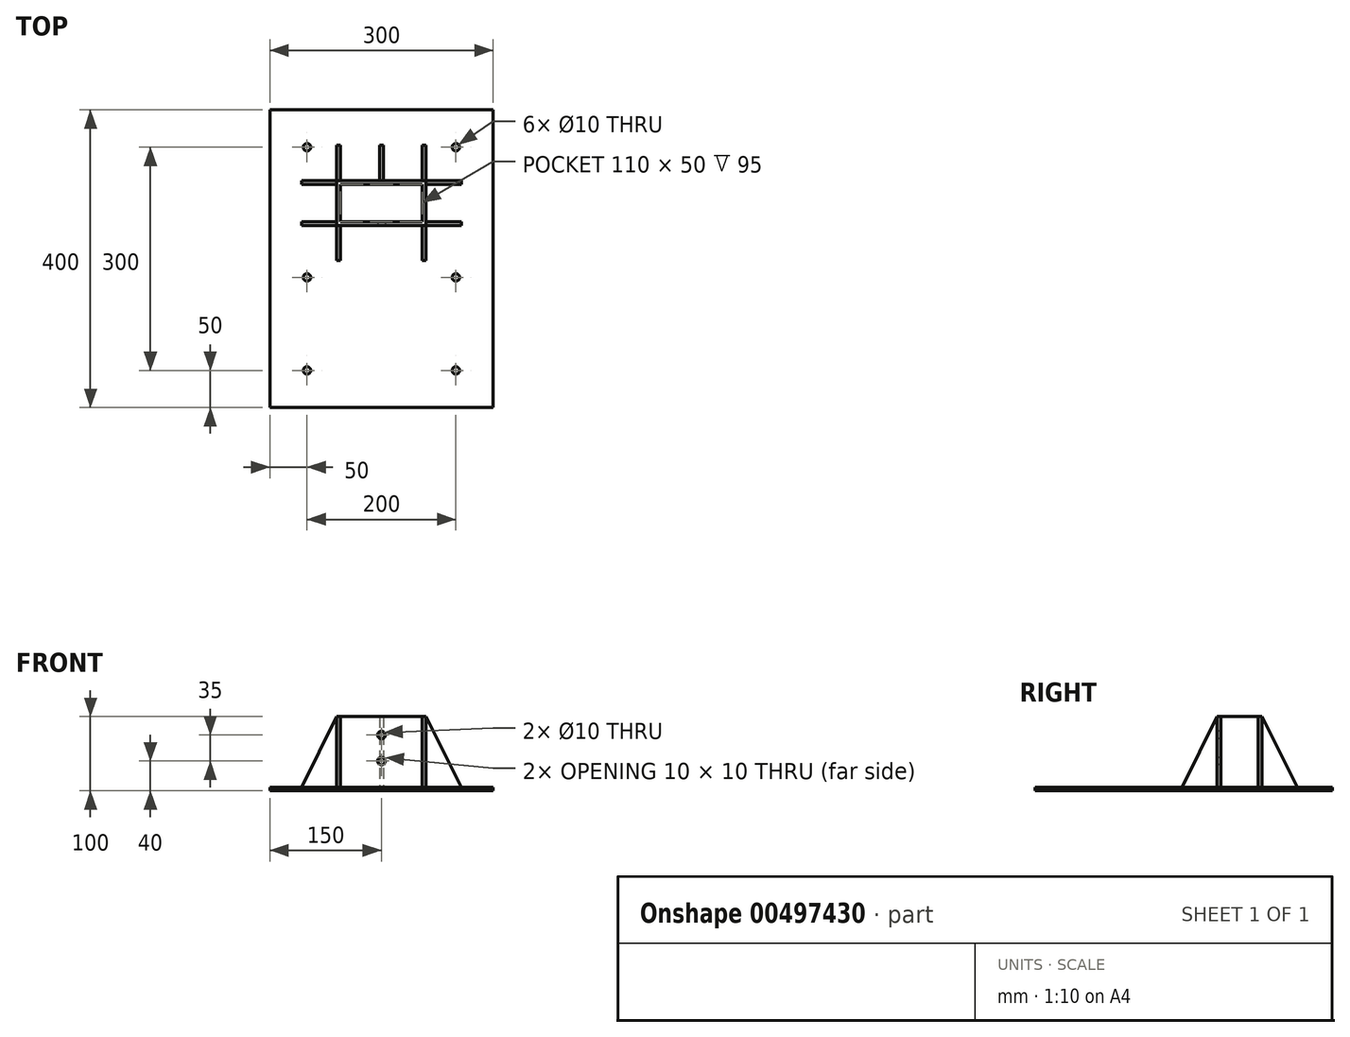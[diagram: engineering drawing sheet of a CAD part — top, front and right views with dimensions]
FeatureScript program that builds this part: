
annotation { "Feature Type Name" : "Feature", "Feature Type Description" : "" }
export const myFeature = defineFeature(function(context is Context, id is Id, definition is map)
    precondition{}
    {
        {
            var Q0;
            Q0=qCreatedBy(makeId("Top.planeOp"),FACE);
            var sketch = newSketch(context, id + "F0", { "sketchPlane" : qUnion([Q0])});
            skLineSegment(sketch, "E0.bottom", {"start": v(-150, -200) * mm, "end": v(150, -200) * mm});
            skLineSegment(sketch, "E0.top", {"start": v(-150, 200) * mm, "end": v(150, 200) * mm});
            skLineSegment(sketch, "E0.left", {"start": v(-150, -200) * mm, "end": v(-150, 200) * mm});
            skLineSegment(sketch, "E0.right", {"start": v(150, -200) * mm, "end": v(150, 200) * mm});
            skPoint(sketch, "E0.middle", {"position": v(0, 0) * mm});
            skLineSegment(sketch, "E1.bottom", {"start": v(-55, 50) * mm, "end": v(55, 50) * mm});
            skLineSegment(sketch, "E1.top", {"start": v(-55, 100) * mm, "end": v(55, 100) * mm});
            skLineSegment(sketch, "E1.left", {"start": v(-55, 50) * mm, "end": v(-55, 100) * mm});
            skLineSegment(sketch, "E1.right", {"start": v(55, 50) * mm, "end": v(55, 100) * mm});
            skPoint(sketch, "E1.middle", {"position": v(0, 75) * mm});
            skLineSegment(sketch, "E2.bottom", {"start": v(60, 45) * mm, "end": v(-60, 45) * mm});
            skLineSegment(sketch, "E2.top", {"start": v(60, 105) * mm, "end": v(-60, 105) * mm});
            skLineSegment(sketch, "E2.left", {"start": v(60, 45) * mm, "end": v(60, 105) * mm});
            skLineSegment(sketch, "E2.right", {"start": v(-60, 45) * mm, "end": v(-60, 105) * mm});
            skLineSegment(sketch, "E3", {"start": v(60, 105) * mm, "end": v(60, 155) * mm});
            skLineSegment(sketch, "E4", {"start": v(60, 155) * mm, "end": v(55, 155) * mm});
            skLineSegment(sketch, "E5", {"start": v(55, 155) * mm, "end": v(55, 100) * mm});
            skLineSegment(sketch, "E6", {"start": v(-60, 105) * mm, "end": v(-60, 155) * mm});
            skLineSegment(sketch, "E7", {"start": v(-60, 155) * mm, "end": v(-55, 155) * mm});
            skLineSegment(sketch, "E8", {"start": v(-55, 155) * mm, "end": v(-55, 100) * mm});
            skLineSegment(sketch, "E9", {"start": v(60, 105) * mm, "end": v(110, 105) * mm});
            skLineSegment(sketch, "E10", {"start": v(110, 105) * mm, "end": v(110, 100) * mm});
            skLineSegment(sketch, "E11", {"start": v(110, 100) * mm, "end": v(55, 100) * mm});
            skLineSegment(sketch, "E12", {"start": v(60, 45) * mm, "end": v(110, 45) * mm});
            skLineSegment(sketch, "E13", {"start": v(110, 45) * mm, "end": v(110, 50) * mm});
            skLineSegment(sketch, "E14", {"start": v(110, 50) * mm, "end": v(55, 50) * mm});
            skLineSegment(sketch, "E15", {"start": v(60, 45) * mm, "end": v(60, -5) * mm});
            skLineSegment(sketch, "E16", {"start": v(60, -5) * mm, "end": v(55, -5) * mm});
            skLineSegment(sketch, "E17", {"start": v(55, -5) * mm, "end": v(55, 50) * mm});
            skLineSegment(sketch, "E18", {"start": v(-60, 45) * mm, "end": v(-60, -5) * mm});
            skLineSegment(sketch, "E19", {"start": v(-60, -5) * mm, "end": v(-55, -5) * mm});
            skLineSegment(sketch, "E20", {"start": v(-55, -5) * mm, "end": v(-55, 50) * mm});
            skLineSegment(sketch, "E21", {"start": v(-60, 45) * mm, "end": v(-110, 45) * mm});
            skLineSegment(sketch, "E22", {"start": v(-110, 45) * mm, "end": v(-110, 50) * mm});
            skLineSegment(sketch, "E23", {"start": v(-110, 50) * mm, "end": v(-55, 50) * mm});
            skLineSegment(sketch, "E24", {"start": v(-60, 105) * mm, "end": v(-110, 105) * mm});
            skLineSegment(sketch, "E25", {"start": v(-110, 105) * mm, "end": v(-110, 100) * mm});
            skLineSegment(sketch, "E26", {"start": v(-110, 100) * mm, "end": v(-55, 100) * mm});
            skPoint(sketch, "E27", {"position": v(100, 150) * mm});
            skPoint(sketch, "E28", {"position": v(-100, 150) * mm});
            skPoint(sketch, "E29", {"position": v(100, -150) * mm});
            skPoint(sketch, "E30", {"position": v(100, -25) * mm});
            skPoint(sketch, "E31", {"position": v(-100, -150) * mm});
            skPoint(sketch, "E32", {"position": v(-100, -25) * mm});
            skLineSegment(sketch, "E33", {"start": v(2.5, 105) * mm, "end": v(2.5, 155) * mm});
            skLineSegment(sketch, "E34", {"start": v(2.5, 155) * mm, "end": v(-2.5, 155) * mm});
            skLineSegment(sketch, "E35", {"start": v(-2.5, 155) * mm, "end": v(-2.5, 105) * mm});
            skSolve(sketch);
        }
        {
            var Q0;
            {var subQ0=sQuery(id+"F0.wireOp",EDGE,"E6");Q0=makeQuery(id+"F0.imprint","IMPRINT",FACE,{"disambiguationData":[TD([[makeQuery(id+"F0.imprint","IMPRINT",EDGE,{"derivedFrom":subQ0}),-1.0]])]});}
            var Q1;
            {var subQ0=sQuery(id+"F0.wireOp",EDGE,"E18");Q1=makeQuery(id+"F0.imprint","IMPRINT",FACE,{"disambiguationData":[TD([[makeQuery(id+"F0.imprint","IMPRINT",EDGE,{"derivedFrom":subQ0}),1.0]])]});}
            var Q2;
            {var subQ1=sQuery(id+"F0.wireOp",EDGE,"E2.top");var subQ3=sQuery(id+"F0.wireOp",EDGE,"E8");var subQ4=makeQuery(id+"F0.imprint","INTERSECT",VERTEX,{"derivedFrom":[subQ1,subQ3]});Q2=makeQuery(id+"F0.imprint","IMPRINT",FACE,{"disambiguationData":[TD([[makeQuery(id+"F0.imprint","IMPRINT",EDGE,{"disambiguationData":[TD([[subQ4,-1.0]])],"derivedFrom":subQ1}),1.0]])]});}
            var Q3;
            {var subQ1=sQuery(id+"F0.wireOp",EDGE,"E2.top");var subQ3=sQuery(id+"F0.wireOp",EDGE,"E5");var subQ4=makeQuery(id+"F0.imprint","INTERSECT",VERTEX,{"derivedFrom":[subQ1,subQ3]});Q3=makeQuery(id+"F0.imprint","IMPRINT",FACE,{"disambiguationData":[TD([[makeQuery(id+"F0.imprint","IMPRINT",EDGE,{"disambiguationData":[TD([[subQ4,1.0]])],"derivedFrom":subQ1}),1.0]])]});}
            var Q4;
            {var subQ0=sQuery(id+"F0.wireOp",EDGE,"E21");Q4=makeQuery(id+"F0.imprint","IMPRINT",FACE,{"disambiguationData":[TD([[makeQuery(id+"F0.imprint","IMPRINT",EDGE,{"derivedFrom":subQ0}),-1.0]])]});}
            var Q5;
            {var subQ0=sQuery(id+"F0.wireOp",EDGE,"E24");Q5=makeQuery(id+"F0.imprint","IMPRINT",FACE,{"disambiguationData":[TD([[makeQuery(id+"F0.imprint","IMPRINT",EDGE,{"derivedFrom":subQ0}),1.0]])]});}
            var Q6;
            {var subQ0=sQuery(id+"F0.wireOp",EDGE,"E1.top");Q6=makeQuery(id+"F0.imprint","IMPRINT",FACE,{"disambiguationData":[TD([[makeQuery(id+"F0.imprint","IMPRINT",EDGE,{"derivedFrom":subQ0}),1.0]])]});}
            var Q7;
            {var subQ1=sQuery(id+"F0.wireOp",EDGE,"E2.bottom");var subQ3=sQuery(id+"F0.wireOp",EDGE,"E17");var subQ4=makeQuery(id+"F0.imprint","INTERSECT",VERTEX,{"derivedFrom":[subQ1,subQ3]});Q7=makeQuery(id+"F0.imprint","IMPRINT",FACE,{"disambiguationData":[TD([[makeQuery(id+"F0.imprint","IMPRINT",EDGE,{"disambiguationData":[TD([[subQ4,1.0]])],"derivedFrom":subQ1}),-1.0]])]});}
            var Q8;
            {var subQ0=sQuery(id+"F0.wireOp",EDGE,"E1.right");Q8=makeQuery(id+"F0.imprint","IMPRINT",FACE,{"disambiguationData":[TD([[makeQuery(id+"F0.imprint","IMPRINT",EDGE,{"derivedFrom":subQ0}),-1.0]])]});}
            var Q9;
            {var subQ0=sQuery(id+"F0.wireOp",EDGE,"E1.bottom");Q9=makeQuery(id+"F0.imprint","IMPRINT",FACE,{"disambiguationData":[TD([[makeQuery(id+"F0.imprint","IMPRINT",EDGE,{"derivedFrom":subQ0}),-1.0]])]});}
            var Q10;
            {var subQ0=sQuery(id+"F0.wireOp",EDGE,"E3");Q10=makeQuery(id+"F0.imprint","IMPRINT",FACE,{"disambiguationData":[TD([[makeQuery(id+"F0.imprint","IMPRINT",EDGE,{"derivedFrom":subQ0}),1.0]])]});}
            var Q11;
            {var subQ0=sQuery(id+"F0.wireOp",EDGE,"E9");Q11=makeQuery(id+"F0.imprint","IMPRINT",FACE,{"disambiguationData":[TD([[makeQuery(id+"F0.imprint","IMPRINT",EDGE,{"derivedFrom":subQ0}),-1.0]])]});}
            var Q12;
            {var subQ1=sQuery(id+"F0.wireOp",EDGE,"E2.bottom");var subQ3=sQuery(id+"F0.wireOp",EDGE,"E20");var subQ4=makeQuery(id+"F0.imprint","INTERSECT",VERTEX,{"derivedFrom":[subQ1,subQ3]});Q12=makeQuery(id+"F0.imprint","IMPRINT",FACE,{"disambiguationData":[TD([[makeQuery(id+"F0.imprint","IMPRINT",EDGE,{"disambiguationData":[TD([[subQ4,-1.0]])],"derivedFrom":subQ1}),-1.0]])]});}
            var Q13;
            {var subQ0=sQuery(id+"F0.wireOp",EDGE,"E12");Q13=makeQuery(id+"F0.imprint","IMPRINT",FACE,{"disambiguationData":[TD([[makeQuery(id+"F0.imprint","IMPRINT",EDGE,{"derivedFrom":subQ0}),1.0]])]});}
            var Q14;
            {var subQ0=sQuery(id+"F0.wireOp",EDGE,"E1.left");Q14=makeQuery(id+"F0.imprint","IMPRINT",FACE,{"disambiguationData":[TD([[makeQuery(id+"F0.imprint","IMPRINT",EDGE,{"derivedFrom":subQ0}),1.0]])]});}
            var Q15;
            {var subQ0=sQuery(id+"F0.wireOp",EDGE,"E15");Q15=makeQuery(id+"F0.imprint","IMPRINT",FACE,{"disambiguationData":[TD([[makeQuery(id+"F0.imprint","IMPRINT",EDGE,{"derivedFrom":subQ0}),-1.0]])]});}
            var Q16;
            {var subQ0=sQuery(id+"F0.wireOp",EDGE,"E33");Q16=makeQuery(id+"F0.imprint","IMPRINT",FACE,{"disambiguationData":[TD([[makeQuery(id+"F0.imprint","IMPRINT",EDGE,{"derivedFrom":subQ0}),1.0]])]});}
            extrude(context, id + "F1", {"entities" : qUnion([Q0, Q1, Q2, Q3, Q4, Q5, Q6, Q7, Q8, Q9, Q10, Q11, Q12, Q13, Q14, Q15, Q16]), "depth" : 100 * mm});
        }
        {
            var Q0;
            Q0 = qSketchRegion(id + "F0", true);
            var Q1;
            Q1=makeQuery(id+"F0.imprint","IMPRINT",FACE,{"disambiguationData":[TD([[makeQuery(id+"F0.imprint","IMPRINT",EDGE,{"derivedFrom":sQuery(id+"F0.wireOp",EDGE,"E1.bottom")}),1.0]])]});
            extrude(context, id + "F2", {"entities" : qUnion([Q0, Q1]), "operationType" : NewBodyOperationType.ADD, "depth" : 5 * mm});
        }
        {
            var Q0;
            Q0=makeQuery(id+"F1.opExtrude","CAP_EDGE",EDGE,{"disambiguationData":[OSD([sQuery(id+"F0.wireOp",EDGE,"E13")])],"isStart":false});
            var Q1;
            Q1=makeQuery(id+"F1.opExtrude","CAP_EDGE",EDGE,{"disambiguationData":[OSD([sQuery(id+"F0.wireOp",EDGE,"E10")])],"isStart":false});
            var Q2;
            Q2=makeQuery(id+"F1.opExtrude","CAP_EDGE",EDGE,{"disambiguationData":[OSD([sQuery(id+"F0.wireOp",EDGE,"E16")])],"isStart":false});
            var Q3;
            Q3=makeQuery(id+"F1.opExtrude","CAP_EDGE",EDGE,{"disambiguationData":[OSD([sQuery(id+"F0.wireOp",EDGE,"E4")])],"isStart":false});
            var Q4;
            Q4=makeQuery(id+"F1.opExtrude","CAP_EDGE",EDGE,{"disambiguationData":[OSD([sQuery(id+"F0.wireOp",EDGE,"E19")])],"isStart":false});
            var Q5;
            Q5=makeQuery(id+"F1.opExtrude","CAP_EDGE",EDGE,{"disambiguationData":[OSD([sQuery(id+"F0.wireOp",EDGE,"E22")])],"isStart":false});
            var Q6;
            Q6=makeQuery(id+"F1.opExtrude","CAP_EDGE",EDGE,{"disambiguationData":[OSD([sQuery(id+"F0.wireOp",EDGE,"E25")])],"isStart":false});
            var Q7;
            Q7=makeQuery(id+"F1.opExtrude","CAP_EDGE",EDGE,{"disambiguationData":[OSD([sQuery(id+"F0.wireOp",EDGE,"E7")])],"isStart":false});
            var Q8;
            Q8=makeQuery(id+"F1.opExtrude","CAP_EDGE",EDGE,{"disambiguationData":[OSD([sQuery(id+"F0.wireOp",EDGE,"E34")])],"isStart":false});
            chamfer(context, id + "F3", {"entities" : qUnion([Q0, Q1, Q2, Q3, Q4, Q5, Q6, Q7, Q8]), "chamferType" : ChamferType.TWO_OFFSETS, "width1" : 50 * mm, "oppositeDirection" : false, "width2" : 100 * mm, "tangentPropagation" : true});
        }
        {
            var Q0;
            Q0=qCreatedBy(makeId("Front.planeOp"),FACE);
            cPlane(context, id + "F4", {"entities" : qUnion([Q0]), "cplaneType" : CPlaneType.OFFSET, "offset" : 45 * mm, "oppositeDirection" : true, "width" : 150 * mm, "height" : 150 * mm});
        }
        {
            var Q0;
            Q0=qCreatedBy(id+"F4.planeOp",FACE);
            var sketch = newSketch(context, id + "F5", { "sketchPlane" : qUnion([Q0])});
            skPoint(sketch, "E36", {"position": v(0, 40) * mm});
            skPoint(sketch, "E37", {"position": v(0, 75) * mm});
            skSolve(sketch);
        }
        {
            var Q0;
            Q0=sQuery(id+"F5.wireOp",VERTEX,"E36");
            var Q1;
            Q1=sQuery(id+"F5.wireOp",VERTEX,"E37");
            var Q2;
            Q2=makeQuery(id+"F1.opExtrude","SWEPT_BODY",BODY,{"disambiguationData":[OSD([sQuery(id+"F0.wireOp",EDGE,"E1.bottom"),sQuery(id+"F0.wireOp",EDGE,"E1.top"),sQuery(id+"F0.wireOp",EDGE,"E1.left"),sQuery(id+"F0.wireOp",EDGE,"E1.right"),sQuery(id+"F0.wireOp",EDGE,"E2.bottom"),sQuery(id+"F0.wireOp",EDGE,"E2.top"),sQuery(id+"F0.wireOp",EDGE,"E2.left"),sQuery(id+"F0.wireOp",EDGE,"E2.right"),sQuery(id+"F0.wireOp",EDGE,"E3"),sQuery(id+"F0.wireOp",EDGE,"E4"),sQuery(id+"F0.wireOp",EDGE,"E5"),sQuery(id+"F0.wireOp",EDGE,"E6"),sQuery(id+"F0.wireOp",EDGE,"E7"),sQuery(id+"F0.wireOp",EDGE,"E8"),sQuery(id+"F0.wireOp",EDGE,"E9"),sQuery(id+"F0.wireOp",EDGE,"E10"),sQuery(id+"F0.wireOp",EDGE,"E11"),sQuery(id+"F0.wireOp",EDGE,"E12"),sQuery(id+"F0.wireOp",EDGE,"E13"),sQuery(id+"F0.wireOp",EDGE,"E14"),sQuery(id+"F0.wireOp",EDGE,"E15"),sQuery(id+"F0.wireOp",EDGE,"E16"),sQuery(id+"F0.wireOp",EDGE,"E17"),sQuery(id+"F0.wireOp",EDGE,"E18"),sQuery(id+"F0.wireOp",EDGE,"E19"),sQuery(id+"F0.wireOp",EDGE,"E20"),sQuery(id+"F0.wireOp",EDGE,"E21"),sQuery(id+"F0.wireOp",EDGE,"E22"),sQuery(id+"F0.wireOp",EDGE,"E23"),sQuery(id+"F0.wireOp",EDGE,"E24"),sQuery(id+"F0.wireOp",EDGE,"E25"),sQuery(id+"F0.wireOp",EDGE,"E26"),sQuery(id+"F0.wireOp",EDGE,"E33"),sQuery(id+"F0.wireOp",EDGE,"E34"),sQuery(id+"F0.wireOp",EDGE,"E35")])]});
            hole(context, id + "F6", {"style" : HoleStyle.SIMPLE, "endStyle" : HoleEndStyle.BLIND, "holeDiameter" : 10 * mm, "holeDepth" : 20 * mm, "isTappedThrough" : true, "tappedDepth" : 12 * mm, "tapClearance" : 3, "startFromSketch" : true, "locations" : qUnion([Q0, Q1]), "scope" : qUnion([Q2])});
        }
        {
            var Q0;
            Q0=sQuery(id+"F0.wireOp",VERTEX,"E32");
            var Q1;
            Q1=sQuery(id+"F0.wireOp",VERTEX,"E28");
            var Q2;
            Q2=sQuery(id+"F0.wireOp",VERTEX,"E27");
            var Q3;
            Q3=sQuery(id+"F0.wireOp",VERTEX,"E30");
            var Q4;
            Q4=sQuery(id+"F0.wireOp",VERTEX,"E29");
            var Q5;
            Q5=sQuery(id+"F0.wireOp",VERTEX,"E31");
            var Q6;
            Q6=makeQuery(id+"F1.opExtrude","SWEPT_BODY",BODY,{"disambiguationData":[OSD([sQuery(id+"F0.wireOp",EDGE,"E1.bottom"),sQuery(id+"F0.wireOp",EDGE,"E1.top"),sQuery(id+"F0.wireOp",EDGE,"E1.left"),sQuery(id+"F0.wireOp",EDGE,"E1.right"),sQuery(id+"F0.wireOp",EDGE,"E2.bottom"),sQuery(id+"F0.wireOp",EDGE,"E2.top"),sQuery(id+"F0.wireOp",EDGE,"E2.left"),sQuery(id+"F0.wireOp",EDGE,"E2.right"),sQuery(id+"F0.wireOp",EDGE,"E3"),sQuery(id+"F0.wireOp",EDGE,"E4"),sQuery(id+"F0.wireOp",EDGE,"E5"),sQuery(id+"F0.wireOp",EDGE,"E6"),sQuery(id+"F0.wireOp",EDGE,"E7"),sQuery(id+"F0.wireOp",EDGE,"E8"),sQuery(id+"F0.wireOp",EDGE,"E9"),sQuery(id+"F0.wireOp",EDGE,"E10"),sQuery(id+"F0.wireOp",EDGE,"E11"),sQuery(id+"F0.wireOp",EDGE,"E12"),sQuery(id+"F0.wireOp",EDGE,"E13"),sQuery(id+"F0.wireOp",EDGE,"E14"),sQuery(id+"F0.wireOp",EDGE,"E15"),sQuery(id+"F0.wireOp",EDGE,"E16"),sQuery(id+"F0.wireOp",EDGE,"E17"),sQuery(id+"F0.wireOp",EDGE,"E18"),sQuery(id+"F0.wireOp",EDGE,"E19"),sQuery(id+"F0.wireOp",EDGE,"E20"),sQuery(id+"F0.wireOp",EDGE,"E21"),sQuery(id+"F0.wireOp",EDGE,"E22"),sQuery(id+"F0.wireOp",EDGE,"E23"),sQuery(id+"F0.wireOp",EDGE,"E24"),sQuery(id+"F0.wireOp",EDGE,"E25"),sQuery(id+"F0.wireOp",EDGE,"E26"),sQuery(id+"F0.wireOp",EDGE,"E33"),sQuery(id+"F0.wireOp",EDGE,"E34"),sQuery(id+"F0.wireOp",EDGE,"E35")])]});
            hole(context, id + "F7", {"style" : HoleStyle.SIMPLE, "endStyle" : HoleEndStyle.BLIND, "oppositeDirection" : true, "holeDiameter" : 10 * mm, "holeDepth" : 20 * mm, "isTappedThrough" : true, "tappedDepth" : 12 * mm, "tapClearance" : 3, "startFromSketch" : true, "locations" : qUnion([Q0, Q1, Q2, Q3, Q4, Q5]), "scope" : qUnion([Q6])});
        }
    });
